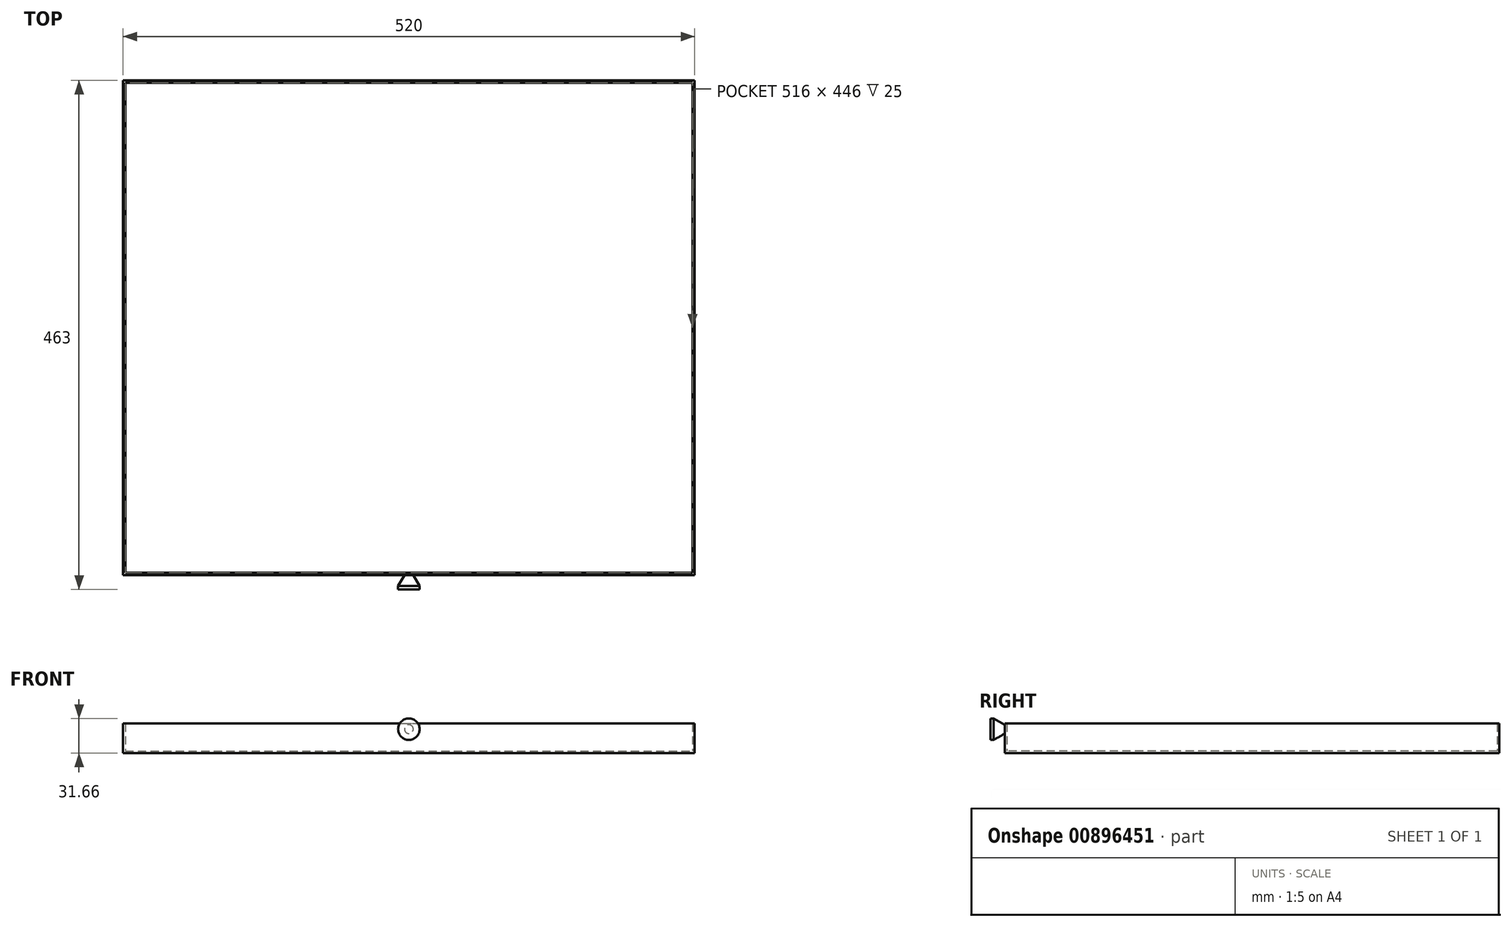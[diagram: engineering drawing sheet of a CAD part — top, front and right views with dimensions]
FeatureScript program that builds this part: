
annotation { "Feature Type Name" : "Feature", "Feature Type Description" : "" }
export const myFeature = defineFeature(function(context is Context, id is Id, definition is map)
    precondition{}
    {
        {
            var Q0;
            Q0=qCreatedBy(makeId("Top.planeOp"),FACE);
            var sketch = newSketch(context, id + "F0", { "sketchPlane" : qUnion([Q0])});
            skLineSegment(sketch, "E0.bottom", {"start": v(-460.68, 177.52) * mm, "end": v(59.32, 177.52) * mm});
            skLineSegment(sketch, "E0.top", {"start": v(-460.68, -272.48) * mm, "end": v(59.32, -272.48) * mm});
            skLineSegment(sketch, "E0.left", {"start": v(-460.68, 177.52) * mm, "end": v(-460.68, -272.48) * mm});
            skLineSegment(sketch, "E0.right", {"start": v(59.32, 177.52) * mm, "end": v(59.32, -272.48) * mm});
            skSolve(sketch);
        }
        {
            var Q0;
            Q0=makeQuery(id+"F0.imprint","IMPRINT",FACE,{"disambiguationData":[TD([[makeQuery(id+"F0.imprint","IMPRINT",EDGE,{"derivedFrom":sQuery(id+"F0.wireOp",EDGE,"E0.bottom")}),-1.0]])]});
            extrude(context, id + "F1", {"entities" : qUnion([Q0]), "depth" : 2 * mm, "offsetDistance" : 25 * mm});
        }
        {
            var Q0;
            Q0=makeQuery(id+"F1.opExtrude","CAP_FACE",FACE,{"disambiguationData":[OSD([sQuery(id+"F0.wireOp",EDGE,"E0.bottom"),sQuery(id+"F0.wireOp",EDGE,"E0.top"),sQuery(id+"F0.wireOp",EDGE,"E0.left"),sQuery(id+"F0.wireOp",EDGE,"E0.right")])],"isStart":false});
            var sketch = newSketch(context, id + "F2", { "sketchPlane" : qUnion([Q0])});
            skLineSegment(sketch, "E1.bottom", {"start": v(-460.68, 177.52) * mm, "end": v(59.32, 177.52) * mm});
            skLineSegment(sketch, "E1.top", {"start": v(-460.68, -272.48) * mm, "end": v(59.32, -272.48) * mm});
            skLineSegment(sketch, "E1.left", {"start": v(-460.68, 177.52) * mm, "end": v(-460.68, -272.48) * mm});
            skLineSegment(sketch, "E1.right", {"start": v(59.32, 177.52) * mm, "end": v(59.32, -272.48) * mm});
            skLineSegment(sketch, "E2.bottom", {"start": v(-458.68, 175.52) * mm, "end": v(57.32, 175.52) * mm});
            skLineSegment(sketch, "E2.top", {"start": v(-458.68, -270.48) * mm, "end": v(57.32, -270.48) * mm});
            skLineSegment(sketch, "E2.left", {"start": v(-458.68, 175.52) * mm, "end": v(-458.68, -270.48) * mm});
            skLineSegment(sketch, "E2.right", {"start": v(57.32, 175.52) * mm, "end": v(57.32, -270.48) * mm});
            skSolve(sketch);
        }
        {
            var Q0;
            Q0=makeQuery(id+"F2.imprint","IMPRINT",FACE,{"disambiguationData":[TD([[makeQuery(id+"F2.imprint","IMPRINT",EDGE,{"derivedFrom":sQuery(id+"F2.wireOp",EDGE,"E1.bottom")}),-1.0]])]});
            extrude(context, id + "F3", {"entities" : qUnion([Q0]), "operationType" : NewBodyOperationType.ADD, "depth" : 25 * mm, "offsetDistance" : 25 * mm});
        }
        {
            var Q0;
            Q0=makeQuery(id+"F3.boolean.opBoolean","MERGE",FACE,{"derivedFrom":[makeQuery(id+"F1.opExtrude","SWEPT_FACE",FACE,{"disambiguationData":[OSD([sQuery(id+"F0.wireOp",EDGE,"E0.top")])]}),makeQuery(id+"F3.opExtrude","SWEPT_FACE",FACE,{"disambiguationData":[OSD([sQuery(id+"F2.wireOp",EDGE,"E1.top")])]})]});
            var sketch = newSketch(context, id + "F4", { "sketchPlane" : qUnion([Q0])});
            skCircle(sketch, "E3", {"center": v(-200.68, 21.89) * mm, "radius": 4 * mm});
            skPoint(sketch, "E3.centerSnap0", {"position": v(-200.68, 27) * mm});
            skSolve(sketch);
        }
        {
            var Q0;
            Q0=makeQuery(id+"F4.imprint","IMPRINT",FACE,{"disambiguationData":[TD([[makeQuery(id+"F4.imprint","IMPRINT",EDGE,{"derivedFrom":sQuery(id+"F4.wireOp",EDGE,"E3")}),1.0]])]});
            var Q1;
            Q1=sQuery(id+"F4.wireOp",EDGE,"E3");
            extrude(context, id + "F5", {"entities" : qUnion([Q0]), "operationType" : NewBodyOperationType.ADD, "surfaceOperationType" : NewSurfaceOperationType.ADD, "surfaceEntities" : qUnion([Q1]), "depth" : 10 * mm, "offsetDistance" : 25 * mm, "hasDraft" : true, "draftAngle" : 30 * degree});
        }
        {
            var Q0;
            Q0=makeQuery(id+"F5.opExtrude","CAP_FACE",FACE,{"disambiguationData":[OSD([sQuery(id+"F4.wireOp",EDGE,"E3")])],"isStart":false});
            extrude(context, id + "F6", {"entities" : qUnion([Q0]), "depth" : 3 * mm, "offsetDistance" : 25 * mm});
        }
    });
